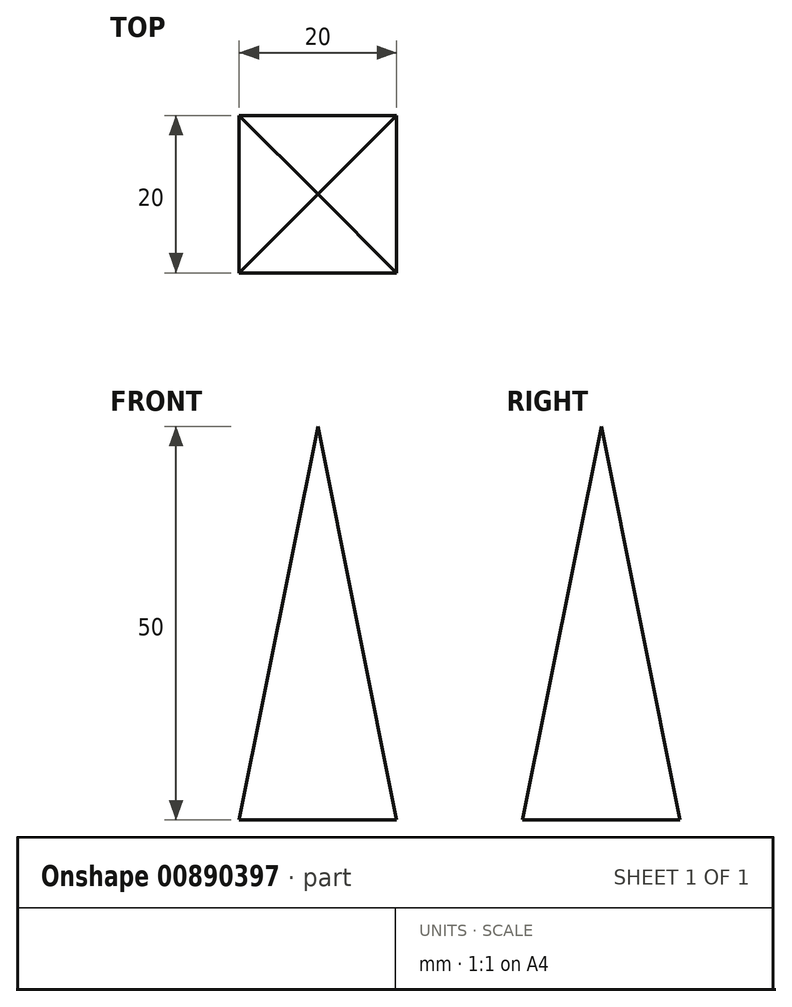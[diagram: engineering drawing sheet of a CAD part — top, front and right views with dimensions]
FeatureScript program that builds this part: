
annotation { "Feature Type Name" : "Feature", "Feature Type Description" : "" }
export const myFeature = defineFeature(function(context is Context, id is Id, definition is map)
    precondition{}
    {
        {
            var Q0;
            Q0=qCreatedBy(makeId("Top.planeOp"),FACE);
            var sketch = newSketch(context, id + "F0", { "sketchPlane" : qUnion([Q0])});
            skLineSegment(sketch, "E0.bottom", {"start": v(-10, -10) * mm, "end": v(10, -10) * mm});
            skLineSegment(sketch, "E0.top", {"start": v(-10, 10) * mm, "end": v(10, 10) * mm});
            skLineSegment(sketch, "E0.left", {"start": v(-10, -10) * mm, "end": v(-10, 10) * mm});
            skLineSegment(sketch, "E0.right", {"start": v(10, -10) * mm, "end": v(10, 10) * mm});
            skPoint(sketch, "E0.middle", {"position": v(0, 0) * mm});
            skSolve(sketch);
        }
        {
            var Q0;
            Q0=makeQuery(id+"F0.imprint","IMPRINT",FACE,{"disambiguationData":[TD([[makeQuery(id+"F0.imprint","IMPRINT",EDGE,{"derivedFrom":sQuery(id+"F0.wireOp",EDGE,"E0.bottom")}),1.0]])]});
            extrude(context, id + "F1", {"entities" : qUnion([Q0]), "depth" : 50 * mm, "offsetDistance" : 25 * mm});
        }
        {
            var Q0;
            Q0=makeQuery(id+"F1.opExtrude","SWEPT_FACE",FACE,{"disambiguationData":[OSD([sQuery(id+"F0.wireOp",EDGE,"E0.bottom")])]});
            var sketch = newSketch(context, id + "F2", { "sketchPlane" : qUnion([Q0])});
            skLineSegment(sketch, "E1.0", {"start": v(-10, 0) * mm, "end": v(10, 0) * mm});
            skLineSegment(sketch, "E1.1", {"start": v(-10, 50) * mm, "end": v(10, 50) * mm});
            skLineSegment(sketch, "E1.2", {"start": v(10, 50) * mm, "end": v(10, 0) * mm});
            skLineSegment(sketch, "E1.3", {"start": v(-10, 50) * mm, "end": v(-10, 0) * mm});
            skLineSegment(sketch, "E2", {"start": v(10, 0) * mm, "end": v(0, 50) * mm});
            skLineSegment(sketch, "E3", {"start": v(0, 50) * mm, "end": v(-10, 0) * mm});
            skSolve(sketch);
        }
        {
            var Q0;
            {var subQ0=sQuery(id+"F2.wireOp",EDGE,"E1.3");Q0=makeQuery(id+"F2.imprint","IMPRINT",FACE,{"disambiguationData":[TD([[makeQuery(id+"F2.imprint","IMPRINT",EDGE,{"derivedFrom":subQ0}),1.0]])]});}
            var Q1;
            {var subQ0=sQuery(id+"F2.wireOp",EDGE,"E1.2");Q1=makeQuery(id+"F2.imprint","IMPRINT",FACE,{"disambiguationData":[TD([[makeQuery(id+"F2.imprint","IMPRINT",EDGE,{"derivedFrom":subQ0}),-1.0]])]});}
            extrude(context, id + "F3", {"entities" : qUnion([Q0, Q1]), "operationType" : NewBodyOperationType.REMOVE, "oppositeDirection" : true, "depth" : 25 * mm, "offsetDistance" : 25 * mm});
        }
        {
            var Q0;
            Q0=qCreatedBy(makeId("Right.planeOp"),FACE);
            var sketch = newSketch(context, id + "F4", { "sketchPlane" : qUnion([Q0])});
            skLineSegment(sketch, "E4.0", {"start": v(-10, 0) * mm, "end": v(10, 0) * mm});
            skLineSegment(sketch, "E4.1", {"start": v(10, 50) * mm, "end": v(-10, 50) * mm});
            skLineSegment(sketch, "E4.2", {"start": v(10, 50) * mm, "end": v(10, 0) * mm});
            skLineSegment(sketch, "E4.3", {"start": v(-10, 0) * mm, "end": v(-10, 50) * mm});
            skLineSegment(sketch, "E5", {"start": v(10, 0) * mm, "end": v(0, 50) * mm});
            skLineSegment(sketch, "E6", {"start": v(0, 50) * mm, "end": v(-10, 0) * mm});
            skSolve(sketch);
        }
        {
            var Q0;
            {var subQ0=sQuery(id+"F4.wireOp",EDGE,"E4.2");Q0=makeQuery(id+"F4.imprint","IMPRINT",FACE,{"disambiguationData":[TD([[makeQuery(id+"F4.imprint","IMPRINT",EDGE,{"derivedFrom":subQ0}),-1.0]])]});}
            var Q1;
            {var subQ0=sQuery(id+"F4.wireOp",EDGE,"E4.3");Q1=makeQuery(id+"F4.imprint","IMPRINT",FACE,{"disambiguationData":[TD([[makeQuery(id+"F4.imprint","IMPRINT",EDGE,{"derivedFrom":subQ0}),-1.0]])]});}
            extrude(context, id + "F5", {"entities" : qUnion([Q0, Q1]), "operationType" : NewBodyOperationType.REMOVE, "endBound" : BoundingType.SYMMETRIC, "oppositeDirection" : true, "depth" : 25 * mm, "offsetDistance" : 25 * mm});
        }
    });
